# Revit family: STL22735BR_PTO_30
name_source: partatom
category: Luminárias
units: mm (PartAtom-declared; Revit-internal decimal feet)

## family parameters
Compartilhado = Não
Corte com vazios quando carregada = Não
Cota do conector redondo = Utilizar diâmetro
Fonte luminosa = Sim
Hospedeiro = Parede
Manter orientação da anotação = Não
Número OmniClass = 23.80.70.00
Ponto de cálculo do ambiente = Não
Sempre na vertical = Sim
Tipo de parte = Normal
Título OmniClass = Lighting

## types (2) — shared parameters
Altura = 0.14 m
Comprimento = 0.12 m
Dimerização = Não dimerizável
Fabricante = Stella
Filtro de cor = 16777215
Fluxo Luminoso = 40 lm
Grau de proteção (IP) = IP65
IRC (Índice de reprodução de cores) = >80
Largura = 0.04 m
Luminoso = Luminoso - 3000K
Modelo = Wall Plus
Potência = 10 W
Temperatura da cor (K) = 3000 K
Tensão Elétrica = 100V-240V
Troca de temperatura da cor de lâmpada com esmaecimento = <Nenhum>
URL = https://stella.com.br
Vidro = Vidro
Ângulo de Abertura = 2°/2°
Ângulo de inclinação = 90.00°
zero-valued in all types: Elevação padrão

## per-type parameters (varying)
| type | Arquivo de rede fotométrica | Estrutura | Referência |
| STH22735BR/30 - BRANCO - BIVOLT - 3000K - 40lm | STL22735BR-30 - WALL PLUS - 2 FACHOS FECHADOS - FACHO 1.ies | Al - Branco | STH22735BR/30 |
| STH22735PTO/30 - PRETO - BIVOLT - 3000K - 40lm | STL22735BR-30 - WALL PLUS - 2 FACHOS FECHADOS - FACHO 2.ies | Al - Preto | STH22735PTO/30 |
